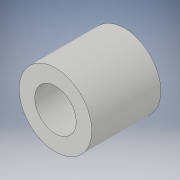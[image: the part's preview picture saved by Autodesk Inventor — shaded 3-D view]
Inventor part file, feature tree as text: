
AUTODESK INVENTOR PART (.ipt)
format: ipt  version: 2018 (Build 220112000, 112)  size: 97,280 bytes
history: native  units: in
note: dims shown in document units (in); Inventor stores cm internally (conversion verified against a paired STEP export)
features: extrude x1, sketch x1
ambient origin geometry x8: Origin, YZ Plane, XZ Plane, XY Plane, X Axis, Y Axis, Z Axis, Center Point
bodies: Solid1 (feature_tree)
feature tree (2):
  extrude  "Extrusion1"  Depth=4.75in
  sketch  "Sketch1"  dims[d0=2.85in d1=5.0in d2=4.75in d3=0.0in]
